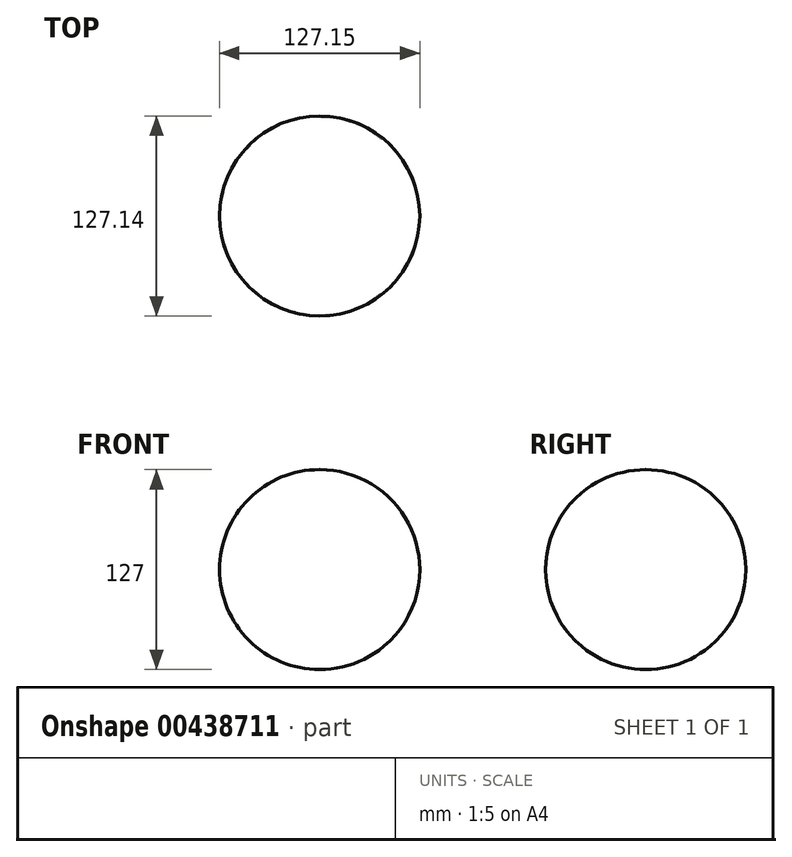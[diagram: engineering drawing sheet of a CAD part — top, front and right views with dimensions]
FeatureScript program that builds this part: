
annotation { "Feature Type Name" : "Feature", "Feature Type Description" : "" }
export const myFeature = defineFeature(function(context is Context, id is Id, definition is map)
    precondition{}
    {
        {
            var Q0;
            Q0=qCreatedBy(makeId("Front.planeOp"),FACE);
            var sketch = newSketch(context, id + "F0", { "sketchPlane" : qUnion([Q0])});
            skLineSegment(sketch, "E0", {"start": v(-17.12, -48.47) * mm, "end": v(-17.12, 78.53) * mm});
            skArc(sketch, "E1", {"start": v(-17.12, -48.47) * mm, "mid": v(46.46, 15.03) * mm, "end": v(-17.12, 78.53) * mm});
            skLineSegment(sketch, "E2", {"start": v(-17.12, 78.53) * mm, "end": v(-17.12, -48.47) * mm});
            skLineSegment(sketch, "E3", {"start": v(-17.12, -48.47) * mm, "end": v(-17.12, 106.83) * mm});
            skSolve(sketch);
        }
        {
            var Q0;
            {var subQ0=sQuery(id+"F0.wireOp",EDGE,"E1");Q0=makeQuery(id+"F0.imprint","IMPRINT",FACE,{"disambiguationData":[TD([[makeQuery(id+"F0.imprint","IMPRINT",EDGE,{"derivedFrom":subQ0}),1.0]])]});}
            var Q1;
            Q1=sQuery(id+"F0.wireOp",EDGE,"E3");
            revolve(context, id + "F1", {"entities" : qUnion([Q0]), "axis" : qUnion([Q1]), "revolveType" : RevolveType.FULL});
        }
    });
